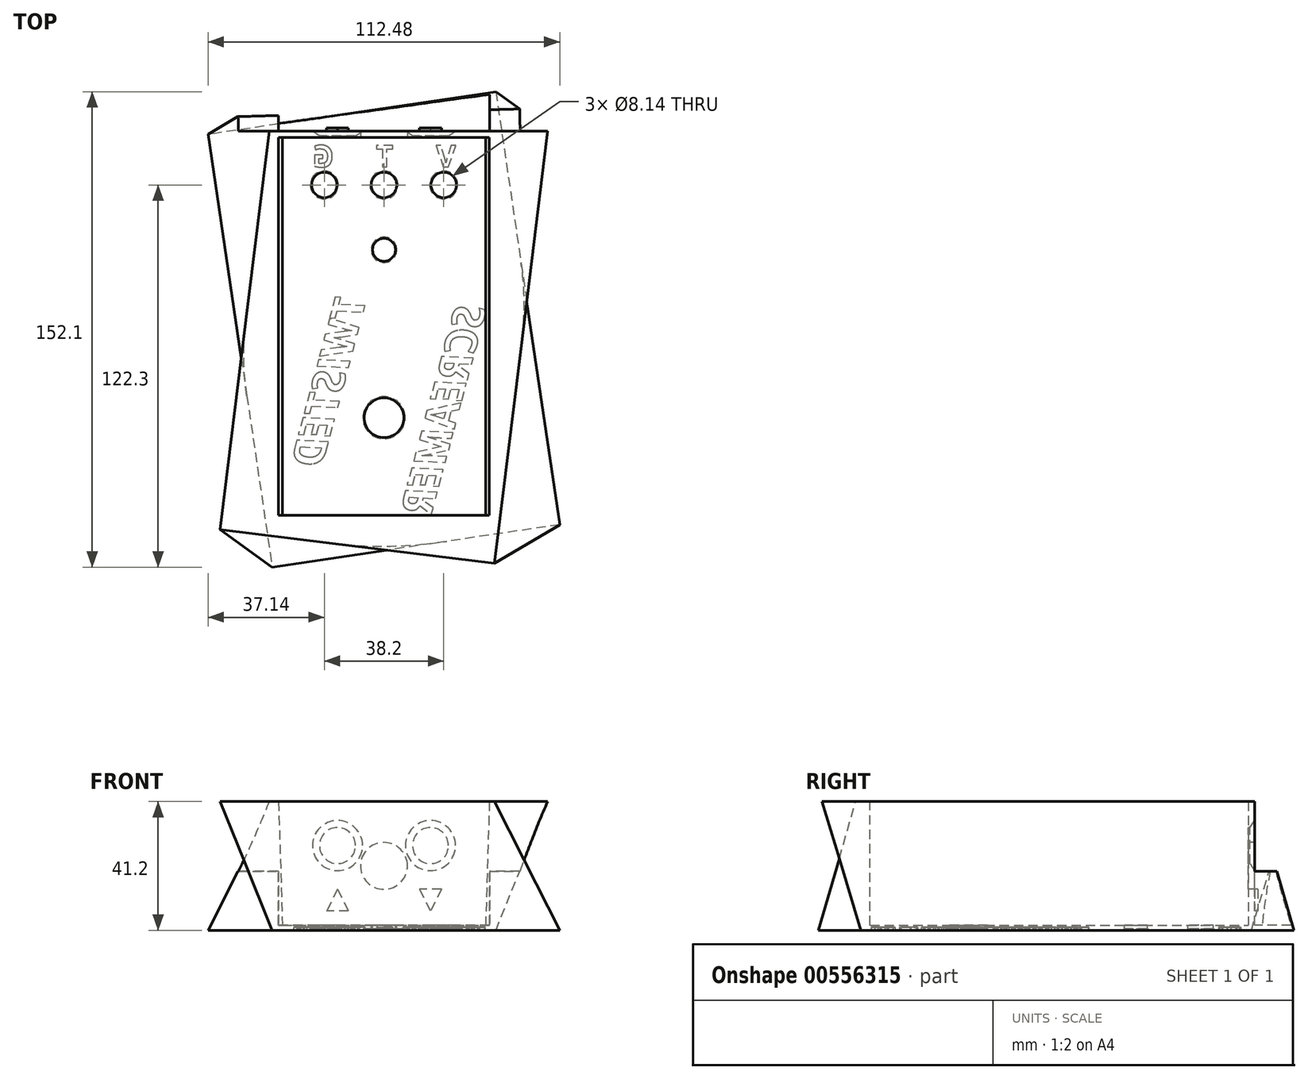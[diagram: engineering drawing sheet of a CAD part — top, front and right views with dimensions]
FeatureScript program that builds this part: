
annotation { "Feature Type Name" : "Feature", "Feature Type Description" : "" }
export const myFeature = defineFeature(function(context is Context, id is Id, definition is map)
    precondition{}
    {
        {
            var Q0;
            Q0=qCreatedBy(makeId("Top.planeOp"),FACE);
            var sketch = newSketch(context, id + "F0", { "sketchPlane" : qUnion([Q0])});
            skLineSegment(sketch, "E0.bottom", {"start": v(-36.5, 64) * mm, "end": v(36.5, 64) * mm});
            skLineSegment(sketch, "E0.top", {"start": v(-36.5, -64) * mm, "end": v(36.5, -64) * mm});
            skLineSegment(sketch, "E0.left", {"start": v(-36.5, 64) * mm, "end": v(-36.5, -64) * mm});
            skLineSegment(sketch, "E0.right", {"start": v(36.5, 64) * mm, "end": v(36.5, -64) * mm});
            skSolve(sketch);
        }
        {
            var Q0;
            Q0=makeQuery(id+"F0.imprint","IMPRINT",FACE,{"disambiguationData":[TD([[makeQuery(id+"F0.imprint","IMPRINT",EDGE,{"derivedFrom":sQuery(id+"F0.wireOp",EDGE,"E0.bottom")}),-1.0]])]});
            extrude(context, id + "F1", {"entities" : qUnion([Q0]), "depth" : 41.2 * mm, "offsetDistance" : 25 * mm});
        }
        {
            var Q0;
            {var subQ0=sQuery(id+"F0.wireOp",EDGE,"E0.bottom");var subQ1=sQuery(id+"F0.wireOp",EDGE,"E0.left");var subQ2=sQuery(id+"F0.wireOp",EDGE,"E0.top");var subQ3=sQuery(id+"F0.wireOp",EDGE,"E0.right");Q0=makeQuery(id+"F16.boolean.opBoolean","SPLIT",FACE,{"disambiguationData":[TD([makeQuery(id+"F1.opExtrude","SWEPT_FACE",FACE,{"disambiguationData":[OSD([subQ0])]})])],"derivedFrom":makeQuery(id+"F1.opExtrude","CAP_FACE",FACE,{"disambiguationData":[OSD([subQ0,subQ2,subQ1,subQ3])],"isStart":true})});}
            var sketch = newSketch(context, id + "F2", { "sketchPlane" : qUnion([Q0])});
            skLineSegment(sketch, "E1.bottom", {"start": v(35.76, -75.05) * mm, "end": v(-56.24, -61.45) * mm});
            skLineSegment(sketch, "E1.top", {"start": v(56.24, 63.45) * mm, "end": v(-35.76, 77.05) * mm});
            skLineSegment(sketch, "E1.left", {"start": v(35.76, -75.05) * mm, "end": v(56.24, 63.45) * mm});
            skLineSegment(sketch, "E1.right", {"start": v(-56.24, -61.45) * mm, "end": v(-35.76, 77.05) * mm});
            skPoint(sketch, "E1.middle", {"position": v(0, 1) * mm});
            skSolve(sketch);
        }
        {
            var Q0;
            Q0=makeQuery(id+"F1.opExtrude","CAP_FACE",FACE,{"disambiguationData":[OSD([sQuery(id+"F0.wireOp",EDGE,"E0.bottom"),sQuery(id+"F0.wireOp",EDGE,"E0.top"),sQuery(id+"F0.wireOp",EDGE,"E0.left"),sQuery(id+"F0.wireOp",EDGE,"E0.right")])],"isStart":false});
            var sketch = newSketch(context, id + "F3", { "sketchPlane" : qUnion([Q0])});
            skLineSegment(sketch, "E2.bottom", {"start": v(-35.35, 73.87) * mm, "end": v(52.41, 63.1) * mm});
            skLineSegment(sketch, "E2.top", {"start": v(-52.41, -65.1) * mm, "end": v(35.35, -75.87) * mm});
            skLineSegment(sketch, "E2.left", {"start": v(-35.35, 73.87) * mm, "end": v(-52.41, -65.1) * mm});
            skLineSegment(sketch, "E2.right", {"start": v(52.41, 63.1) * mm, "end": v(35.35, -75.87) * mm});
            skPoint(sketch, "E2.middle", {"position": v(0, -1) * mm});
            skSolve(sketch);
        }
        {
            var Q1;
            Q1=qSketchRegion(id+"F2",true);
            var Q2;
            Q2=qSketchRegion(id+"F3",true);
            var Q3;
            Q3=sQuery(id+"F2.wireOp",VERTEX,"E1.left.start");
            var Q4;
            Q4=sQuery(id+"F3.wireOp",VERTEX,"E2.right.start");
            loft(context, id + "F4", {"operationType" : NewBodyOperationType.ADD, "sheetProfilesArray" : [{ "sheetProfileEntities" : qUnion([Q1]) }, { "sheetProfileEntities" : qUnion([Q2]) }], "matchConnections" : true, "connections" : [{ "connectionEntities" : qUnion([Q3, Q4]), "connectionEdgeQueries" : qUnion([]), "connectionEdgeParameters" : [] }]});
        }
        {
            var Q0;
            Q0=makeQuery(id+"F1.opExtrude","CAP_FACE",FACE,{"disambiguationData":[OSD([sQuery(id+"F0.wireOp",EDGE,"E0.bottom"),sQuery(id+"F0.wireOp",EDGE,"E0.top"),sQuery(id+"F0.wireOp",EDGE,"E0.left"),sQuery(id+"F0.wireOp",EDGE,"E0.right")])],"isStart":false});
            var sketch = newSketch(context, id + "F5", { "sketchPlane" : qUnion([Q0])});
            skLineSegment(sketch, "E3.bottom", {"start": v(-33.75, 60.5) * mm, "end": v(33.75, 60.5) * mm});
            skLineSegment(sketch, "E3.top", {"start": v(-33.75, -60.5) * mm, "end": v(33.75, -60.5) * mm});
            skLineSegment(sketch, "E3.left", {"start": v(-33.75, 60.5) * mm, "end": v(-33.75, -60.5) * mm});
            skLineSegment(sketch, "E3.right", {"start": v(33.75, 60.5) * mm, "end": v(33.75, -60.5) * mm});
            skSolve(sketch);
        }
        {
            var Q0;
            Q0=makeQuery(id+"F5.imprint","IMPRINT",FACE,{"disambiguationData":[TD([[makeQuery(id+"F5.imprint","IMPRINT",EDGE,{"derivedFrom":sQuery(id+"F5.wireOp",EDGE,"E3.bottom")}),-1.0]])]});
            extrude(context, id + "F6", {"entities" : qUnion([Q0]), "operationType" : NewBodyOperationType.REMOVE, "oppositeDirection" : true, "depth" : (40.4 - 0.8) * mm, "offsetDistance" : 25 * mm});
        }
        {
            var Q0;
            Q0=makeQuery(id+"F6.boolean.opBoolean","COPY",FACE,{"derivedFrom":makeQuery(id+"F6.opExtrude","CAP_FACE",FACE,{"disambiguationData":[OSD([sQuery(id+"F5.wireOp",EDGE,"E3.bottom"),sQuery(id+"F5.wireOp",EDGE,"E3.top"),sQuery(id+"F5.wireOp",EDGE,"E3.left"),sQuery(id+"F5.wireOp",EDGE,"E3.right")])],"isStart":false})});
            var sketch = newSketch(context, id + "F7", { "sketchPlane" : qUnion([Q0])});
            skCircle(sketch, "E4", {"center": v(-19.1, 45.25) * mm, "radius": 4.07 * mm});
            skCircle(sketch, "E5", {"center": v(0, 45.25) * mm, "radius": 4.07 * mm});
            skCircle(sketch, "E6", {"center": v(19.1, 45.25) * mm, "radius": 4.07 * mm});
            skCircle(sketch, "E7", {"center": v(0, -29.25) * mm, "radius": 6.35 * mm});
            skLineSegment(sketch, "E8", {"start": v(19.1, 45.25) * mm, "end": v(0, 45.25) * mm, "construction": true});
            skCircle(sketch, "E9", {"center": v(0, 24.5) * mm, "radius": 3.67 * mm});
            skSolve(sketch);
        }
        {
            var Q0;
            Q0=qSketchRegion(id+"F7",true);
            extrude(context, id + "F8", {"entities" : qUnion([Q0]), "operationType" : NewBodyOperationType.REMOVE, "oppositeDirection" : true, "depth" : 25 * mm, "offsetDistance" : 25 * mm});
        }
        {
            var Q0;
            Q0=makeQuery(id+"F6.boolean.opBoolean","COPY",FACE,{"derivedFrom":makeQuery(id+"F6.opExtrude","SWEPT_FACE",FACE,{"disambiguationData":[OSD([sQuery(id+"F5.wireOp",EDGE,"E3.bottom")])]})});
            cPlane(context, id + "F9", {"entities" : qUnion([Q0]), "cplaneType" : CPlaneType.OFFSET, "offset" : 2 * mm, "oppositeDirection" : true, "width" : 150 * mm, "height" : 150 * mm});
        }
        {
            var Q0;
            Q0=qCreatedBy(id+"F9.planeOp",FACE);
            var sketch = newSketch(context, id + "F10", { "sketchPlane" : qUnion([Q0])});
            skCircle(sketch, "E10", {"center": v(0, 20.6) * mm, "radius": 7.5 * mm});
            skCircle(sketch, "E11", {"center": v(14.87, 27.1) * mm, "radius": 5.76 * mm});
            skCircle(sketch, "E12", {"center": v(-14.88, 27.1) * mm, "radius": 5.76 * mm});
            skSolve(sketch);
        }
        {
            var Q0;
            Q0=qSketchRegion(id+"F10",true);
            extrude(context, id + "F11", {"entities" : qUnion([Q0]), "operationType" : NewBodyOperationType.REMOVE, "endBound" : BoundingType.SYMMETRIC, "oppositeDirection" : true, "depth" : 30 * mm, "offsetDistance" : 25 * mm});
        }
        {
            var Q0;
            Q0=qCreatedBy(id+"F9.planeOp",FACE);
            var sketch = newSketch(context, id + "F12", { "sketchPlane" : qUnion([Q0])});
            skLineSegment(sketch, "E13.0", {"start": v(-33.75, 1.6) * mm, "end": v(-33.75, 41.2) * mm});
            skLineSegment(sketch, "E14.0", {"start": v(-33.75, 1.6) * mm, "end": v(33.75, 1.6) * mm});
            skLineSegment(sketch, "E15.0", {"start": v(33.75, 1.6) * mm, "end": v(33.75, 41.2) * mm});
            skLineSegment(sketch, "E16.0", {"start": v(-33.75, 41.2) * mm, "end": v(33.75, 41.2) * mm});
            skSolve(sketch);
        }
        {
            var Q0;
            Q0=qSketchRegion(id+"F12",true);
            extrude(context, id + "F13", {"entities" : qUnion([Q0]), "operationType" : NewBodyOperationType.REMOVE, "oppositeDirection" : true, "depth" : 25 * mm, "offsetDistance" : 25 * mm});
        }
        {
            var Q0;
            Q0=qCreatedBy(makeId("Front.planeOp"),FACE);
            cPlane(context, id + "F14", {"entities" : qUnion([Q0]), "cplaneType" : CPlaneType.OFFSET, "offset" : 38 * mm, "width" : 150 * mm, "height" : 150 * mm});
        }
        {
            var Q0;
            Q0=makeQuery(id+"F1.opExtrude","CAP_FACE",FACE,{"disambiguationData":[OSD([sQuery(id+"F0.wireOp",EDGE,"E0.bottom"),sQuery(id+"F0.wireOp",EDGE,"E0.top"),sQuery(id+"F0.wireOp",EDGE,"E0.left"),sQuery(id+"F0.wireOp",EDGE,"E0.right")])],"isStart":true});
            var sketch = newSketch(context, id + "F15", { "sketchPlane" : qUnion([Q0])});
            skText(sketch, "E17", { "text": "V", "fontName": "OpenSans-Bold.ttf"});
            skText(sketch, "E18", { "text": "T", "fontName": "OpenSans-Bold.ttf"});
            skText(sketch, "E19", { "text": "G", "fontName": "OpenSans-Bold.ttf"});
            const initialGuessF15  = {"E17": [0.02295, -0.051, -1, 0, 0.007], "E18": [0.00303, -0.051, -1, 0, 0.007], "E19": [-0.016, -0.051, -1, 0, 0.007]};
            skSetInitialGuess(sketch, initialGuessF15);
            skSolve(sketch);
        }
        {
            var Q0;
            Q0=qSketchRegion(id+"F15",true);
            extrude(context, id + "F16", {"entities" : qUnion([Q0]), "operationType" : NewBodyOperationType.REMOVE, "oppositeDirection" : true, "depth" : 1 * mm, "offsetDistance" : 25 * mm, "flatOperationType" : FlatOperationType.REMOVE, "domain" : OperationDomain.MODEL});
        }
        {
            var Q0;
            Q0=makeQuery(id+"F13.boolean.opBoolean","COPY",FACE,{"derivedFrom":makeQuery(id+"F13.opExtrude","CAP_FACE",FACE,{"disambiguationData":[OSD([sQuery(id+"F12.wireOp",EDGE,"E13.0"),sQuery(id+"F12.wireOp",EDGE,"E14.0"),sQuery(id+"F12.wireOp",EDGE,"E15.0"),sQuery(id+"F12.wireOp",EDGE,"E16.0")])],"isStart":true})});
            var sketch = newSketch(context, id + "F17", { "sketchPlane" : qUnion([Q0])});
            skLineSegment(sketch, "E20", {"start": v(75, 18.86) * mm, "end": v(-75, 18.86) * mm});
            skLineSegment(sketch, "E21", {"start": v(-75, 18.86) * mm, "end": v(-75, 44.5) * mm});
            skLineSegment(sketch, "E22", {"start": v(-75, 44.5) * mm, "end": v(75, 44.5) * mm});
            skLineSegment(sketch, "E23", {"start": v(75, 44.5) * mm, "end": v(75, 18.86) * mm});
            skSolve(sketch);
        }
        {
            var Q0;
            Q0=qSketchRegion(id+"F17",true);
            extrude(context, id + "F18", {"entities" : qUnion([Q0]), "operationType" : NewBodyOperationType.REMOVE, "depth" : 15 * mm, "offsetDistance" : 25 * mm});
        }
        {
            var Q0;
            Q0=makeQuery(id+"F13.boolean.opBoolean","INTERSECT",EDGE,{"derivedFrom":[makeQuery(id+"F11.boolean.opBoolean","COPY",FACE,{"derivedFrom":makeQuery(id+"F11.opExtrude","SWEPT_FACE",FACE,{"disambiguationData":[OSD([sQuery(id+"F10.wireOp",EDGE,"E12")])]})}),makeQuery(id+"F13.opExtrude","CAP_FACE",FACE,{"disambiguationData":[OSD([sQuery(id+"F12.wireOp",EDGE,"E13.0"),sQuery(id+"F12.wireOp",EDGE,"E14.0"),sQuery(id+"F12.wireOp",EDGE,"E15.0"),sQuery(id+"F12.wireOp",EDGE,"E16.0")])],"isStart":true})]});
            var Q1;
            Q1=makeQuery(id+"F13.boolean.opBoolean","INTERSECT",EDGE,{"derivedFrom":[makeQuery(id+"F11.boolean.opBoolean","COPY",FACE,{"derivedFrom":makeQuery(id+"F11.opExtrude","SWEPT_FACE",FACE,{"disambiguationData":[OSD([sQuery(id+"F10.wireOp",EDGE,"E11")])]})}),makeQuery(id+"F13.opExtrude","CAP_FACE",FACE,{"disambiguationData":[OSD([sQuery(id+"F12.wireOp",EDGE,"E13.0"),sQuery(id+"F12.wireOp",EDGE,"E14.0"),sQuery(id+"F12.wireOp",EDGE,"E15.0"),sQuery(id+"F12.wireOp",EDGE,"E16.0")])],"isStart":true})]});
            chamfer(context, id + "F19", {"entities" : qUnion([Q0, Q1]), "chamferType" : ChamferType.TWO_OFFSETS, "width1" : 1.5 * mm, "oppositeDirection" : false, "width2" : 2.25 * mm, "tangentPropagation" : true});
        }
        {
            var Q0;
            {var subQ0=sQuery(id+"F0.wireOp",EDGE,"E0.bottom");var subQ1=sQuery(id+"F0.wireOp",EDGE,"E0.top");var subQ2=sQuery(id+"F0.wireOp",EDGE,"E0.left");var subQ3=sQuery(id+"F0.wireOp",EDGE,"E0.right");Q0=makeQuery(id+"F8.boolean.opBoolean","INTERSECT",EDGE,{"derivedFrom":[makeQuery(id+"F4.boolean.opBoolean","MERGE",FACE,{"derivedFrom":[makeQuery(id+"F1.opExtrude","CAP_FACE",FACE,{"disambiguationData":[OSD([subQ0,subQ1,subQ2,subQ3])],"isStart":true}),makeQuery(id+"F4.opLoft","CAP_FACE",FACE,{"disambiguationData":[OSD([makeQuery(id+"F2.imprint","IMPRINT",FACE,{"disambiguationData":[TD([[makeQuery(id+"F2.imprint","IMPRINT",EDGE,{"derivedFrom":makeQuery(id+"F1.opExtrude","CAP_EDGE",EDGE,{"disambiguationData":[OSD([subQ0])],"isStart":true})}),1.0]])]})])],"isStart":true})]}),makeQuery(id+"F8.opExtrude","SWEPT_FACE",FACE,{"disambiguationData":[OSD([sQuery(id+"F7.wireOp",EDGE,"E6")])]})]});}
            var Q1;
            {var subQ0=sQuery(id+"F0.wireOp",EDGE,"E0.bottom");var subQ1=sQuery(id+"F0.wireOp",EDGE,"E0.top");var subQ2=sQuery(id+"F0.wireOp",EDGE,"E0.left");var subQ3=sQuery(id+"F0.wireOp",EDGE,"E0.right");Q1=makeQuery(id+"F8.boolean.opBoolean","INTERSECT",EDGE,{"derivedFrom":[makeQuery(id+"F4.boolean.opBoolean","MERGE",FACE,{"derivedFrom":[makeQuery(id+"F1.opExtrude","CAP_FACE",FACE,{"disambiguationData":[OSD([subQ0,subQ1,subQ2,subQ3])],"isStart":true}),makeQuery(id+"F4.opLoft","CAP_FACE",FACE,{"disambiguationData":[OSD([makeQuery(id+"F2.imprint","IMPRINT",FACE,{"disambiguationData":[TD([[makeQuery(id+"F2.imprint","IMPRINT",EDGE,{"derivedFrom":makeQuery(id+"F1.opExtrude","CAP_EDGE",EDGE,{"disambiguationData":[OSD([subQ0])],"isStart":true})}),1.0]])]})])],"isStart":true})]}),makeQuery(id+"F8.opExtrude","SWEPT_FACE",FACE,{"disambiguationData":[OSD([sQuery(id+"F7.wireOp",EDGE,"E5")])]})]});}
            var Q2;
            {var subQ0=sQuery(id+"F0.wireOp",EDGE,"E0.bottom");var subQ1=sQuery(id+"F0.wireOp",EDGE,"E0.top");var subQ2=sQuery(id+"F0.wireOp",EDGE,"E0.left");var subQ3=sQuery(id+"F0.wireOp",EDGE,"E0.right");Q2=makeQuery(id+"F8.boolean.opBoolean","INTERSECT",EDGE,{"derivedFrom":[makeQuery(id+"F4.boolean.opBoolean","MERGE",FACE,{"derivedFrom":[makeQuery(id+"F1.opExtrude","CAP_FACE",FACE,{"disambiguationData":[OSD([subQ0,subQ1,subQ2,subQ3])],"isStart":true}),makeQuery(id+"F4.opLoft","CAP_FACE",FACE,{"disambiguationData":[OSD([makeQuery(id+"F2.imprint","IMPRINT",FACE,{"disambiguationData":[TD([[makeQuery(id+"F2.imprint","IMPRINT",EDGE,{"derivedFrom":makeQuery(id+"F1.opExtrude","CAP_EDGE",EDGE,{"disambiguationData":[OSD([subQ0])],"isStart":true})}),1.0]])]})])],"isStart":true})]}),makeQuery(id+"F8.opExtrude","SWEPT_FACE",FACE,{"disambiguationData":[OSD([sQuery(id+"F7.wireOp",EDGE,"E4")])]})]});}
            var Q3;
            {var subQ0=sQuery(id+"F0.wireOp",EDGE,"E0.bottom");var subQ1=sQuery(id+"F0.wireOp",EDGE,"E0.top");var subQ2=sQuery(id+"F0.wireOp",EDGE,"E0.left");var subQ3=sQuery(id+"F0.wireOp",EDGE,"E0.right");Q3=makeQuery(id+"F8.boolean.opBoolean","INTERSECT",EDGE,{"derivedFrom":[makeQuery(id+"F4.boolean.opBoolean","MERGE",FACE,{"derivedFrom":[makeQuery(id+"F1.opExtrude","CAP_FACE",FACE,{"disambiguationData":[OSD([subQ0,subQ1,subQ2,subQ3])],"isStart":true}),makeQuery(id+"F4.opLoft","CAP_FACE",FACE,{"disambiguationData":[OSD([makeQuery(id+"F2.imprint","IMPRINT",FACE,{"disambiguationData":[TD([[makeQuery(id+"F2.imprint","IMPRINT",EDGE,{"derivedFrom":makeQuery(id+"F1.opExtrude","CAP_EDGE",EDGE,{"disambiguationData":[OSD([subQ0])],"isStart":true})}),1.0]])]})])],"isStart":true})]}),makeQuery(id+"F8.opExtrude","SWEPT_FACE",FACE,{"disambiguationData":[OSD([sQuery(id+"F7.wireOp",EDGE,"E9")])]})]});}
            var Q4;
            {var subQ0=sQuery(id+"F0.wireOp",EDGE,"E0.bottom");var subQ1=sQuery(id+"F0.wireOp",EDGE,"E0.top");var subQ2=sQuery(id+"F0.wireOp",EDGE,"E0.left");var subQ3=sQuery(id+"F0.wireOp",EDGE,"E0.right");Q4=makeQuery(id+"F8.boolean.opBoolean","INTERSECT",EDGE,{"derivedFrom":[makeQuery(id+"F4.boolean.opBoolean","MERGE",FACE,{"derivedFrom":[makeQuery(id+"F1.opExtrude","CAP_FACE",FACE,{"disambiguationData":[OSD([subQ0,subQ1,subQ2,subQ3])],"isStart":true}),makeQuery(id+"F4.opLoft","CAP_FACE",FACE,{"disambiguationData":[OSD([makeQuery(id+"F2.imprint","IMPRINT",FACE,{"disambiguationData":[TD([[makeQuery(id+"F2.imprint","IMPRINT",EDGE,{"derivedFrom":makeQuery(id+"F1.opExtrude","CAP_EDGE",EDGE,{"disambiguationData":[OSD([subQ0])],"isStart":true})}),1.0]])]})])],"isStart":true})]}),makeQuery(id+"F8.opExtrude","SWEPT_FACE",FACE,{"disambiguationData":[OSD([sQuery(id+"F7.wireOp",EDGE,"KNiFqmuv-MMCi-B5FO-T3GH-z67XstVQp584")])]})]});}
            var Q5;
            {var subQ0=sQuery(id+"F0.wireOp",EDGE,"E0.bottom");var subQ1=sQuery(id+"F0.wireOp",EDGE,"E0.top");var subQ2=sQuery(id+"F0.wireOp",EDGE,"E0.left");var subQ3=sQuery(id+"F0.wireOp",EDGE,"E0.right");Q5=makeQuery(id+"F8.boolean.opBoolean","INTERSECT",EDGE,{"derivedFrom":[makeQuery(id+"F4.boolean.opBoolean","MERGE",FACE,{"derivedFrom":[makeQuery(id+"F1.opExtrude","CAP_FACE",FACE,{"disambiguationData":[OSD([subQ0,subQ1,subQ2,subQ3])],"isStart":true}),makeQuery(id+"F4.opLoft","CAP_FACE",FACE,{"disambiguationData":[OSD([makeQuery(id+"F2.imprint","IMPRINT",FACE,{"disambiguationData":[TD([[makeQuery(id+"F2.imprint","IMPRINT",EDGE,{"derivedFrom":makeQuery(id+"F1.opExtrude","CAP_EDGE",EDGE,{"disambiguationData":[OSD([subQ0])],"isStart":true})}),1.0]])]})])],"isStart":true})]}),makeQuery(id+"F8.opExtrude","SWEPT_FACE",FACE,{"disambiguationData":[OSD([sQuery(id+"F7.wireOp",EDGE,"E7")])]})]});}
            chamfer(context, id + "F20", {"entities" : qUnion([Q0, Q1, Q2, Q3, Q4, Q5]), "width" : 0.4 * mm, "tangentPropagation" : true});
        }
        {
            var Q0;
            {var subQ0=sQuery(id+"F0.wireOp",EDGE,"E0.bottom");var subQ1=sQuery(id+"F0.wireOp",EDGE,"E0.top");var subQ2=sQuery(id+"F0.wireOp",EDGE,"E0.left");var subQ3=sQuery(id+"F0.wireOp",EDGE,"E0.right");Q0=makeQuery(id+"F4.boolean.opBoolean","MERGE",FACE,{"derivedFrom":[makeQuery(id+"F1.opExtrude","CAP_FACE",FACE,{"disambiguationData":[OSD([subQ0,subQ1,subQ2,subQ3])],"isStart":true}),makeQuery(id+"F4.opLoft","CAP_FACE",FACE,{"disambiguationData":[OSD([makeQuery(id+"F2.imprint","IMPRINT",FACE,{"disambiguationData":[TD([[makeQuery(id+"F2.imprint","IMPRINT",EDGE,{"derivedFrom":makeQuery(id+"F1.opExtrude","CAP_EDGE",EDGE,{"disambiguationData":[OSD([subQ0])],"isStart":true})}),1.0]])]})])],"isStart":true})]});}
            var sketch = newSketch(context, id + "F21", { "sketchPlane" : qUnion([Q0])});
            skText(sketch, "E24", { "text": "  TWISTED\n\nSCREAMER", "fontName": "OpenSans-BoldItalic.ttf"});
            const initialGuessF21  = {"E24": [-0.00375, -0.01526, -0.25882, 0.96593, 0.01]};
            skSetInitialGuess(sketch, initialGuessF21);
            skSolve(sketch);
        }
        {
            var Q0;
            Q0=qSketchRegion(id+"F21",true);
            extrude(context, id + "F22", {"entities" : qUnion([Q0]), "operationType" : NewBodyOperationType.REMOVE, "flatOperationType" : FlatOperationType.REMOVE, "oppositeDirection" : true, "depth" : 1 * mm, "offsetDistance" : 25 * mm, "domain" : OperationDomain.MODEL});
        }
        {
            var Q0;
            Q0=makeQuery(id+"F18.boolean.opBoolean","MERGE",FACE,{"derivedFrom":[makeQuery(id+"F13.boolean.opBoolean","COPY",FACE,{"derivedFrom":makeQuery(id+"F13.opExtrude","CAP_FACE",FACE,{"disambiguationData":[OSD([sQuery(id+"F12.wireOp",EDGE,"E13.0"),sQuery(id+"F12.wireOp",EDGE,"E14.0"),sQuery(id+"F12.wireOp",EDGE,"E15.0"),sQuery(id+"F12.wireOp",EDGE,"E16.0")])],"isStart":true})}),makeQuery(id+"F18.opExtrude","CAP_FACE",FACE,{"disambiguationData":[OSD([sQuery(id+"F17.wireOp",EDGE,"E20"),sQuery(id+"F17.wireOp",EDGE,"E21"),sQuery(id+"F17.wireOp",EDGE,"E22"),sQuery(id+"F17.wireOp",EDGE,"E23")])],"isStart":true})]});
            var sketch = newSketch(context, id + "F23", { "sketchPlane" : qUnion([Q0])});
            skLineSegment(sketch, "E25", {"start": v(14.88, 27.1) * mm, "end": v(14.88, 6.07) * mm, "construction": true});
            skLineSegment(sketch, "E26", {"start": v(-14.87, 27.1) * mm, "end": v(-14.87, 6.07) * mm, "construction": true});
            skLineSegment(sketch, "E27", {"start": v(-18.37, 13.12) * mm, "end": v(-14.87, 13.12) * mm});
            skLineSegment(sketch, "E28", {"start": v(-18.37, 13.12) * mm, "end": v(-14.87, 6.12) * mm});
            skLineSegment(sketch, "E29", {"start": v(14.88, 13.12) * mm, "end": v(18.38, 6.12) * mm});
            skLineSegment(sketch, "E30", {"start": v(18.38, 6.12) * mm, "end": v(14.88, 6.12) * mm});
            skLineSegment(sketch, "E31.MirrorCS", {"start": v(11.38, 6.12) * mm, "end": v(14.88, 6.12) * mm});
            skLineSegment(sketch, "E32.MirrorCS", {"start": v(14.88, 13.12) * mm, "end": v(11.38, 6.12) * mm});
            skLineSegment(sketch, "E33.MirrorCS", {"start": v(-11.37, 13.12) * mm, "end": v(-14.87, 6.12) * mm});
            skLineSegment(sketch, "E34.MirrorCS", {"start": v(-11.37, 13.12) * mm, "end": v(-14.87, 13.12) * mm});
            skSolve(sketch);
        }
        {
            var Q0;
            Q0 = qSketchRegion(id + "F23", true);
            extrude(context, id + "F24", {"entities" : qUnion([Q0]), "operationType" : NewBodyOperationType.ADD, "depth" : 1 * mm, "offsetDistance" : 25 * mm});
        }
        {
            var Q0;
            Q0=makeQuery(id+"F6.boolean.opBoolean","COPY",EDGE,{"derivedFrom":makeQuery(id+"F6.opExtrude","CAP_EDGE",EDGE,{"disambiguationData":[OSD([sQuery(id+"F5.wireOp",EDGE,"E3.left")])],"isStart":false})});
            var Q1;
            Q1=makeQuery(id+"F6.boolean.opBoolean","COPY",EDGE,{"derivedFrom":makeQuery(id+"F6.opExtrude","CAP_EDGE",EDGE,{"disambiguationData":[OSD([sQuery(id+"F5.wireOp",EDGE,"E3.right")])],"isStart":false})});
            chamfer(context, id + "F25", {"entities" : qUnion([Q0, Q1]), "chamferType" : ChamferType.TWO_OFFSETS, "width1" : 1.25 * mm, "oppositeDirection" : false, "width2" : 40.4 * mm, "tangentPropagation" : true});
        }
    });
